# Revit family: ГРЕЕРС Д3
name_source: partatom
category: Modele ogólne
revit_build: Autodesk Revit 2016 (Build: 20150220_1215(x64)
units: mm (PartAtom-declared; Revit-internal decimal feet)

## family parameters
Może być obiektem nadrzędnym dla zbrojenia = Nie
Obiekt nadrzędny = Powierzchnia
Punkt obliczania pomieszczeń = Nie
Tnij formami wycięć po wczytaniu = Nie
Typ części = Normalny
Współdzielony = Nie
Wymiar okrągłego złącza = Użyj średnicy

## types (3) — shared parameters
IP = 54
Model = ГРЕЕРС Д3
Opis = Дестратификатор воздуха
Opis indeksowy = Дестратификатор LEO Д3 производительностью до 7200 м3/ч
Producent = ГРЕЕРС
Sterowanie = Включи/Выключи
URL = www.greers.ru
Вентилятор = Осевой, однофазный, переменного тока с 3-скоростным вентилятором
Вес аппарата = 19.50 kg
Данные продукта = https://greers.ru
Индекс = 22102
Классификация нагрузки = ДВИГАТЕЛЬ
Коэффициент мощности = 1
Материал = ГРЕЕРС-EPP-черный
Напряжение питания = 230 V
Расстояние от перекрытия = 1000 mm  [stored 3.28084 ft]
Стандартное оснащение = Отсутствие
zero-valued in all types: Domyślna rzędna

## per-type parameters (varying)
| type | Макс. потребление тока | Полная мощность | Производительность |
| ГРЕЕРС Д3, 1 скорость | 1 A | 322 VA | 3900.0 m³/h |
| ГРЕЕРС Д3, 2 скорость | 2 A | 345 VA | 6100.0 m³/h |
| ГРЕЕРС Д3, 3 скорость | 2 A | 368 VA | 7200.0 m³/h |

note: [stored X ft] marks values corroborated as IEEE doubles in the binary element streams (Revit-internal decimal feet)

## geometry (parser evidence)
native form markers: Blend x2
no freeform markers — native parametric forms only
